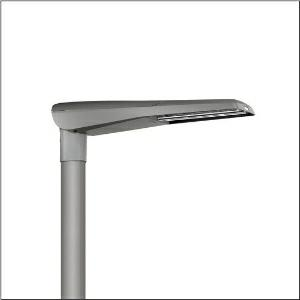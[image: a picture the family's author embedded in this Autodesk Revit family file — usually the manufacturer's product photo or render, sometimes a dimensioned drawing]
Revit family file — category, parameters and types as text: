
# Revit family: streetlight_sl_11_iq_mini___st1_0a_5xc2mc1f08he_59d2
name_source: partatom
category: Lighting Fixtures
units: mm (PartAtom-declared; Revit-internal decimal feet)

## family parameters
Cut with Voids When Loaded = No
Host = Face
Light Source = No
Part Type = Normal
Room Calculation Point = No
Round Connector Dimension = Use Diameter
Shared = No

## types (1)
- --- (1 x LED, 6610 lm, 63.6 W, 2200K)
    Apparent Load = 64 VA
    CIE Flux Codes = 33 66 96 100 100
    Color Rendering = 70
    Color Temperature = 2200K
    Default Elevation = 1800 mm
    Description = Streetlight SL 11 iQ mini, mast luminaire, primary light control with 3 zone facetted reflector, of plastic, silver coated, highly specular, primary optical cover: cover, of PMMA, transparent, light distribution: ST1.0a, light emission: direct distribution, primary light characteristic: asymmetric, installation type: post-top, side-entry, lamps: LED, High Power LED, rated values: 8.070lm | 62,2W | 129,7lm/W (begin service life); end service life: 8.070lm | 65,6W; at 50% lumin. flux: 4.035lm | 29,4W | 137,2lm/W, colour temperature: 2200/2700/3000/4000K, colour rendering: CRI > 70, light colour: 722/727/730/740, light setting 1 begin service life: 100% | 8.070lm | 62,2W | 129,7lm/W | 3.000K, light setting 1 end service life: 65,6W, further light settings possible, control: Street-Remote, Auto-Match, Temp-Guard, Lumen-Switch, Night-Set, Smart-Wire, Light-Fading, Desk-Remote (wireless, voltage-free reading and setting of iQ features in the workshop via application-optimized NFC function/RFID function), optimised constant luminous flux control (CLO 2.0), with cable H07RN-F 3x 1.5mm², mains connection: 230..240V, AC, 50/60Hz, connection cable pre-assembled, cable length: 8,5m, luminaire housing, of diecast aluminium, powder-coated, SITECO metallic grey (DB 702S), please order mast flange separately, inclination adjustable without tools: 0°, 5°, 10°, 15° (post-top) | 0°, -5°, -10°, -15° (side-entry), sealing non-destructively replaceable, multi-level sealing system, length: 736mm, width: 174mm, height: 116mm, mast flange for spigot size: 42mm (side-entry): 5XC10008XM4, 60/48mm (side-entry/post-top): 5XC10108XM2, 76/60mm (side-entry/post-top): 5XC10108XM1, equipment: Power, protection rating (complete): IP66, insulation class (complete): insulation class II (safety insulation), certification: CE, ENEC, ENEC+, VDE, impact resistance: IK10, permissible operating ambient temperature for outdoor applications: -25..+50°C, standard-compliant lighting for roads and squares, Environmental Product Declaration (EPD) tested and certified by an independent institute, packaging unit: 1 piece

Light Distribution: ST1.0a
    Height = 116 mm
    Lamp = 1 x LED
    Lamp Light Flux = 6610 lm
    Lamp Power = 63.6 W
    Lamp count = 1
    Length = 736 mm
    Luminous efficacy = 104 lm/W
    Manufacturer = Siteco
    ModVariant = No
    Model = 5XC2MC1F08HE
    Number of Poles = 1
    OnlyDefault = Yes
    Power Factor = 1
    Product Name = Streetlight SL 11 iQ mini | ST1.0a
    Product group = mast luminaire | pylon top
    ProductGroupID = 6100
    Protection Class = Protection class II
    Protection Degree = IP 66
    RLX_Detail_Level = 1
    RLX_Emergency_Light_Flux = 0 lm
    RLX_Emergency_Type = 0
    RLX_Emergency_Type_DB = No
    RlxData = <blob elided: 53101 chars, md5=d7f54f42>
    Socket = socket
    Standby Power = 0 W
    System Light Flux = 6610 lm
    System Power = 64 W
    Type Comments = individual setting: luminous flux: 100 % | dim-lin: 254 | 866 mA
    Type Image = l_1003508.jpg
    URL = http://relux.com
    VarID = @adj_042337
    Voltage = 0 V
    Weight = 0.00 kg
    Width = 174 mm

## geometry (parser evidence)
native form markers: Blend x4, Sweep x10
no freeform markers — native parametric forms only
